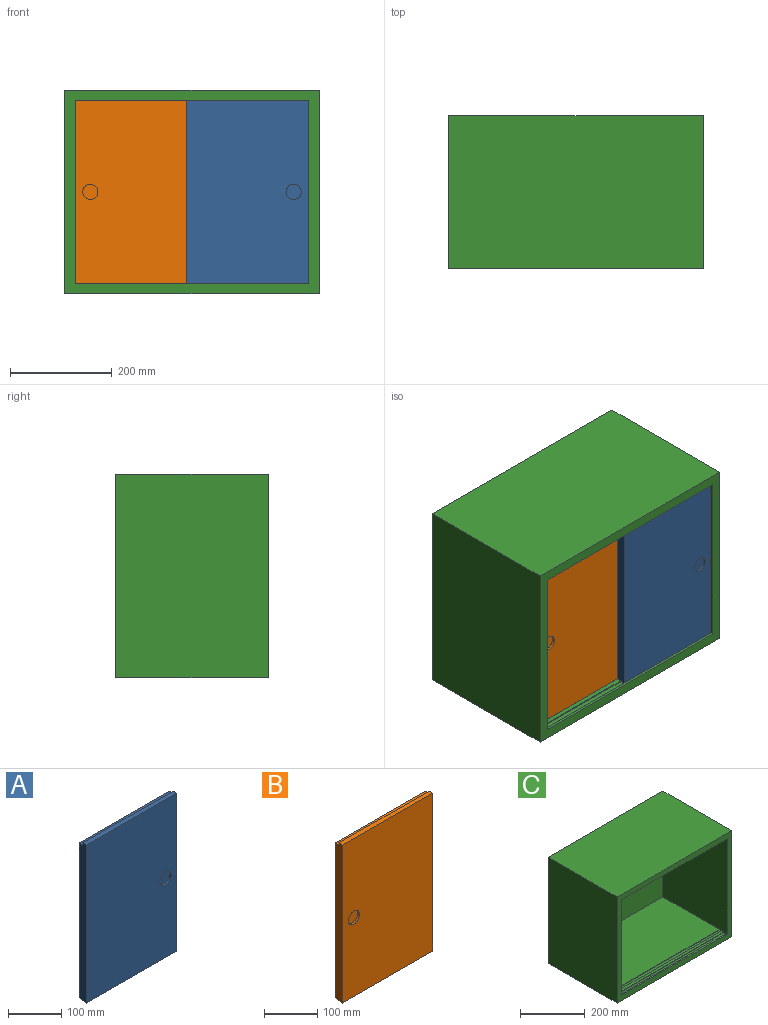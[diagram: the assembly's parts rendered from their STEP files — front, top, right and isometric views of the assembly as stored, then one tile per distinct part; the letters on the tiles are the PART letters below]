
ASSEMBLY  parts=3 mates=2
PART A: 12 faces, bbox 240x20x364.5 mm
  f0: plane 364.5x240mm, normal (0,-1,0), area 86773.1mm2, adj f3,f4,f7,f8,f10
  f1: plane 357.5x240mm, normal (0,1,0), area 85800mm2, adj f3,f6,f7,f9
  f2: plane 240x5mm, normal (0,1,0), area 1200mm2, adj f3,f7,f8,f9
  f3: plane 364.5x20mm, normal (-1,0,0), area 7220mm2, adj f0,f1,f2,f4,f5,f6,f8,f9
  f4: plane 240x10mm, normal (0,0,-1), area 2400mm2, adj f0,f3,f5,f7
  f5: plane 240x2mm, normal (0,1,0), area 480mm2, adj f3,f4,f6,f7
  f6: plane 240x10mm, normal (0,0,-1), area 2400mm2, adj f1,f3,f5,f7
  f7: plane 364.5x20mm, normal (1,0,0), area 7220mm2, adj f0,f1,f2,f4,f5,f6,f8,f9
  f8: plane 240x10mm, normal (0,0,1), area 2400mm2, adj f0,f2,f3,f7
  f9: plane 240x10mm, normal (0,0,1), area 2400mm2, adj f1,f2,f3,f7
  f10: cylinder r=15mm len=30mm, axis (0,-1,0), area 471.2mm2, adj f0,f11
  f11: plane 30x30mm, normal (0,-1,0), area 706.9mm2, adj f10
PART B: 12 faces, bbox 240x20x364.5 mm
  f0: plane 240x5mm, normal (0,1,0), area 1200mm2, adj f2,f3,f8,f9
  f1: plane 364.5x240mm, normal (0,-1,0), area 86773.1mm2, adj f2,f3,f5,f8,f10
  f2: plane 364.5x20mm, normal (1,0,0), area 7220mm2, adj f0,f1,f4,f5,f6,f7,f8,f9
  f3: plane 364.5x20mm, normal (-1,0,0), area 7220mm2, adj f0,f1,f4,f5,f6,f7,f8,f9
  f4: plane 357.5x240mm, normal (0,1,0), area 85800mm2, adj f2,f3,f7,f9
  f5: plane 240x10mm, normal (0,0,-1), area 2400mm2, adj f1,f2,f3,f6
  f6: plane 240x2mm, normal (0,1,0), area 480mm2, adj f2,f3,f5,f7
  f7: plane 240x10mm, normal (0,0,-1), area 2400mm2, adj f2,f3,f4,f6
  f8: plane 240x10mm, normal (0,0,1), area 2400mm2, adj f0,f1,f2,f3
  f9: plane 240x10mm, normal (0,0,1), area 2400mm2, adj f0,f2,f3,f4
  f10: cylinder r=15mm len=30mm, axis (0,-1,0), area 471.2mm2, adj f1,f11
  f11: plane 30x30mm, normal (0,-1,0), area 706.9mm2, adj f10
PART C: 27 faces, bbox 500x300x400 mm
  f0: plane 460x10mm, normal (0,0,-1), area 4600mm2, adj f10,f12,f21,f24
  f1: plane 460x245mm, normal (0,0,-1), area 112700mm2, adj f10,f11,f12,f22
  f2: plane 460x10mm, normal (0,0,1), area 4600mm2, adj f10,f12,f17,f19
  f3: plane 460x245mm, normal (0,0,1), area 112700mm2, adj f10,f11,f12,f16
  f4: plane 500x400mm, normal (0,-1,0), area 34400mm2, adj f5,f7,f8,f9,f10,f12,f13,f14
  f5: plane 400x300mm, normal (1,0,0), area 120000mm2, adj f4,f6,f8,f9
  f6: plane 500x400mm, normal (0,1,0), area 200000mm2, adj f5,f7,f8,f9
  f7: plane 400x300mm, normal (-1,0,0), area 120000mm2, adj f4,f6,f8,f9
  f8: plane 500x300mm, normal (0,0,1), area 150000mm2, adj f4,f5,f6,f7
  f9: plane 500x300mm, normal (0,0,-1), area 150000mm2, adj f4,f5,f6,f7
  f10: plane 367x280mm, normal (-1,0,0), area 100940mm2, adj f0,f1,f2,f3,f4,f11,f13,f14
  f11: plane 460x360mm, normal (0,-1,0), area 165600mm2, adj f1,f3,f10,f12
  f12: plane 367x280mm, normal (1,0,0), area 100940mm2, adj f0,f1,f2,f3,f4,f11,f13,f14
  f13: plane 460x5mm, normal (0,0,-1), area 2300mm2, adj f4,f10,f12,f25
  f14: plane 460x5mm, normal (0,0,1), area 2300mm2, adj f4,f10,f12,f20
  f15: plane 460x10mm, normal (0,0,1), area 4600mm2, adj f10,f12,f16,f17
  f16: plane 460x2mm, normal (0,-1,0), area 920mm2, adj f3,f10,f12,f15
  f17: plane 460x2mm, normal (0,1,0), area 920mm2, adj f2,f10,f12,f15
  f18: plane 460x10mm, normal (0,0,1), area 4600mm2, adj f10,f12,f19,f20
  f19: plane 460x2mm, normal (0,-1,0), area 920mm2, adj f2,f10,f12,f18
  f20: plane 460x2mm, normal (0,1,0), area 920mm2, adj f10,f12,f14,f18
  f21: plane 460x5mm, normal (0,1,0), area 2300mm2, adj f0,f10,f12,f23
  f22: plane 460x5mm, normal (0,-1,0), area 2300mm2, adj f1,f10,f12,f23
  f23: plane 460x10mm, normal (0,0,-1), area 4600mm2, adj f10,f12,f21,f22
  f24: plane 460x5mm, normal (0,-1,0), area 2300mm2, adj f0,f10,f12,f26
  f25: plane 460x5mm, normal (0,1,0), area 2300mm2, adj f10,f12,f13,f26
  f26: plane 460x10mm, normal (0,0,-1), area 4600mm2, adj f10,f12,f24,f25
PLACE A at identity
PLACE B at identity
PLACE C at identity fixed
MATE slider C.f12 <-> B.f3  axis (1,0,0) through (-230,-115,20)mm
MATE slider C.f10 <-> A.f7  axis (-1,0,0) through (230,-135,20)mm
